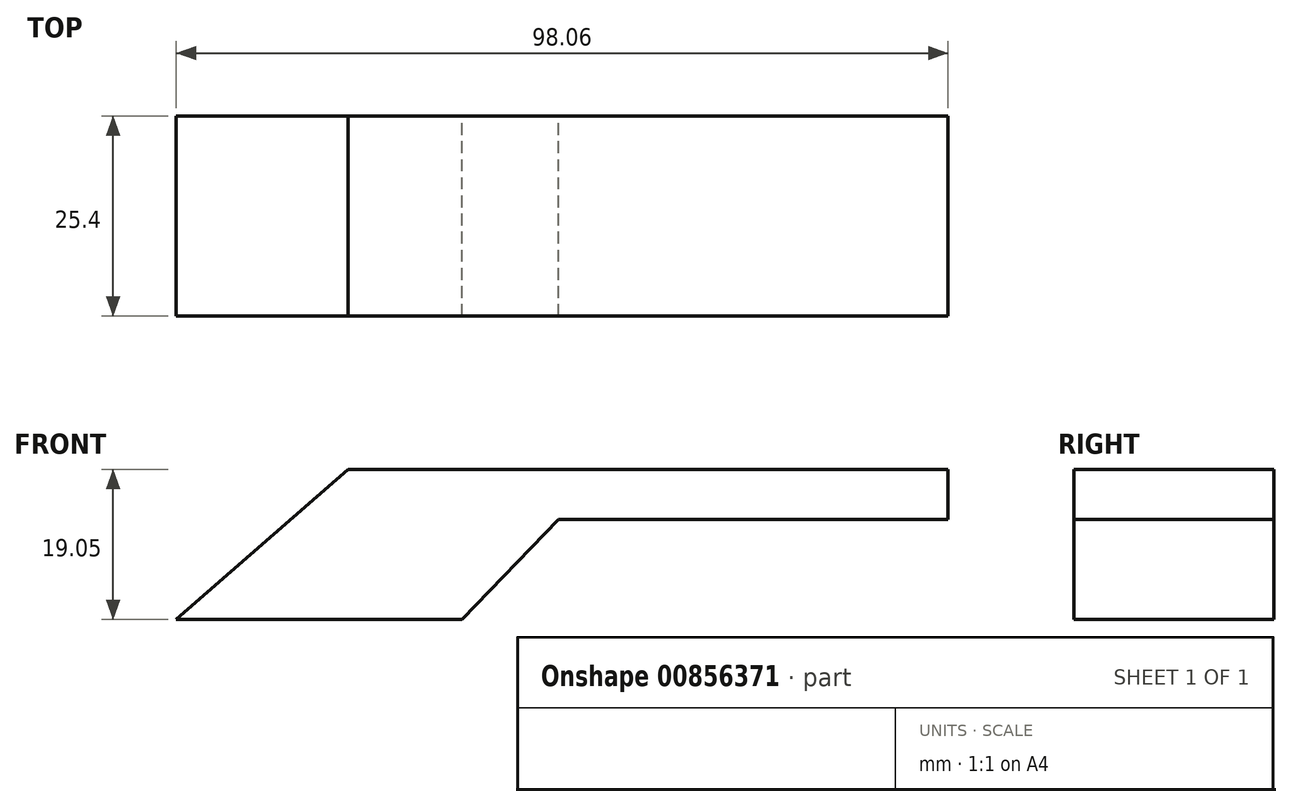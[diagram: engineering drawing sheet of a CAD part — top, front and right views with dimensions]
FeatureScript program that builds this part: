
annotation { "Feature Type Name" : "Feature", "Feature Type Description" : "" }
export const myFeature = defineFeature(function(context is Context, id is Id, definition is map)
    precondition{}
    {
        {
            var Q0;
            Q0=qCreatedBy(makeId("Front.planeOp"),FACE);
            var sketch = newSketch(context, id + "F0", { "sketchPlane" : qUnion([Q0])});
            skLineSegment(sketch, "E0", {"start": v(0, 0) * mm, "end": v(76.2, 0) * mm});
            skLineSegment(sketch, "E1", {"start": v(76.2, 0) * mm, "end": v(0, 0) * mm});
            skLineSegment(sketch, "E2", {"start": v(76.2, 0) * mm, "end": v(76.2, -6.35) * mm});
            skLineSegment(sketch, "E3", {"start": v(76.2, -6.35) * mm, "end": v(26.69, -6.35) * mm});
            skLineSegment(sketch, "E4", {"start": v(0, 0) * mm, "end": v(-21.86, -19.05) * mm});
            skLineSegment(sketch, "E5", {"start": v(-21.86, -19.05) * mm, "end": v(14.47, -19.05) * mm});
            skLineSegment(sketch, "E6", {"start": v(26.69, -6.35) * mm, "end": v(14.47, -19.05) * mm});
            skLineSegment(sketch, "E7", {"start": v(0, 0) * mm, "end": v(-10.93, -19.05) * mm});
            skPoint(sketch, "E7.endSnap0", {"position": v(-3.7, -19.05) * mm});
            skPoint(sketch, "E7.endSnap1", {"position": v(-10.93, -9.53) * mm});
            skSolve(sketch);
        }
        {
            var Q0;
            Q0 = qSketchRegion(id + "F0", true);
            extrude(context, id + "F1", {"entities" : qUnion([Q0]), "depth" : 25.4 * mm, "offsetDistance" : 25.4 * mm});
        }
    });
